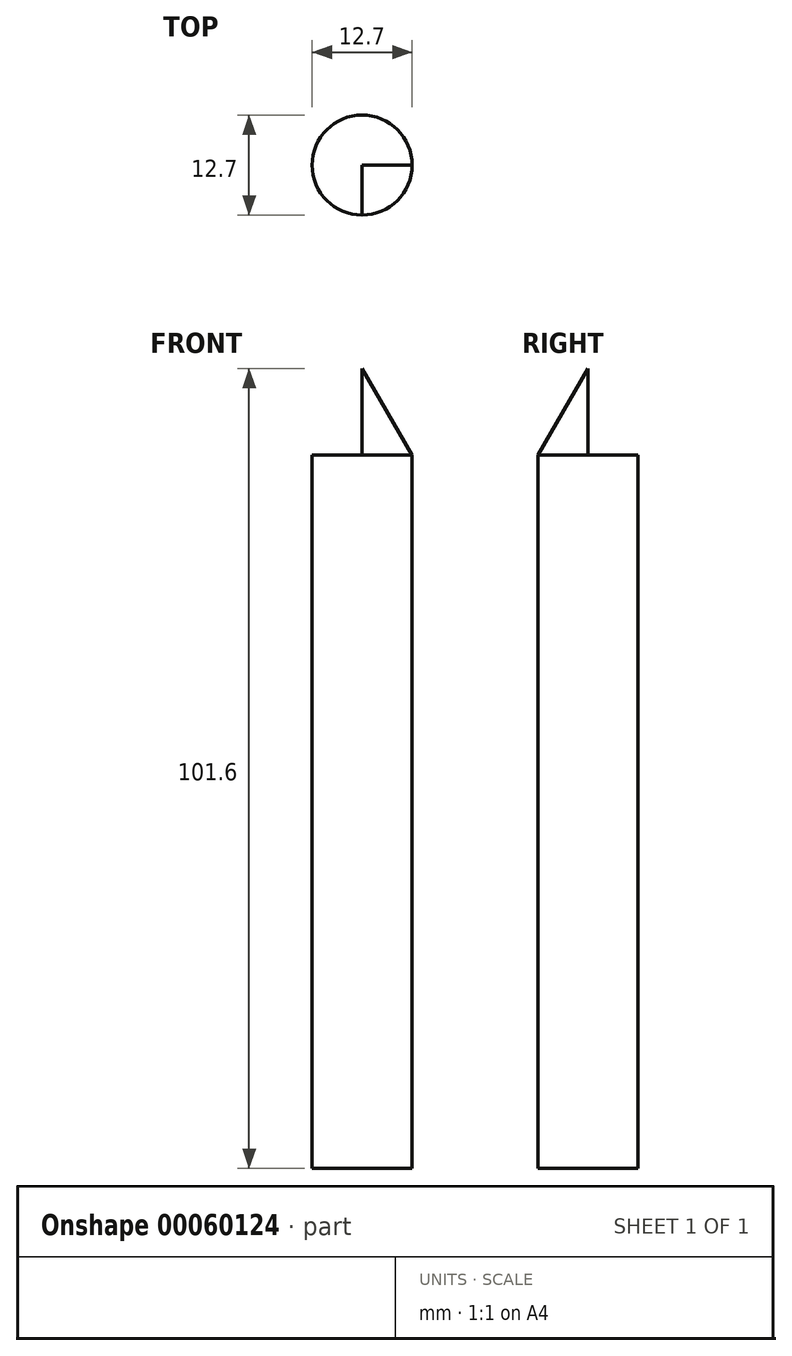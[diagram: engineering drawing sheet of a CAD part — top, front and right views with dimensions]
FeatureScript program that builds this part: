
annotation { "Feature Type Name" : "Feature", "Feature Type Description" : "" }
export const myFeature = defineFeature(function(context is Context, id is Id, definition is map)
    precondition{}
    {
        {
            var Q0;
            Q0=qCreatedBy(makeId("Top.planeOp"),FACE);
            var sketch = newSketch(context, id + "F0", { "sketchPlane" : qUnion([Q0])});
            skCircle(sketch, "E0", {"center": v(0, 0) * mm, "radius": 6.35 * mm});
            skSolve(sketch);
        }
        {
            var Q0;
            Q0 = qSketchRegion(id + "F0", true);
            extrude(context, id + "F1", {"entities" : qUnion([Q0]), "depth" : 50.8 * mm, "hasSecondDirection" : true, "secondDirectionOppositeDirection" : true, "secondDirectionDepth" : 50.8 * mm});
        }
        {
            var Q0;
            Q0=qCreatedBy(makeId("Right.planeOp"),FACE);
            var sketch = newSketch(context, id + "F2", { "sketchPlane" : qUnion([Q0])});
            skLineSegment(sketch, "E1", {"start": v(0, 50.8) * mm, "end": v(-6.35, 39.8) * mm});
            skLineSegment(sketch, "E2", {"start": v(0, 50.8) * mm, "end": v(0, 0) * mm, "construction": true});
            skLineSegment(sketch, "E3", {"start": v(4.5, 58.61) * mm, "end": v(-13.66, 27.15) * mm});
            skLineSegment(sketch, "E4", {"start": v(-13.66, 27.15) * mm, "end": v(-13.66, 58.61) * mm});
            skLineSegment(sketch, "E5", {"start": v(-13.66, 58.61) * mm, "end": v(4.5, 58.61) * mm});
            skLineSegment(sketch, "E6", {"start": v(0, 50.8) * mm, "end": v(0, 58.61) * mm});
            skSolve(sketch);
        }
        {
            var Q0;
            {var subQ0=sQuery(id+"F2.wireOp",EDGE,"E4");Q0=makeQuery(id+"F2.imprint","IMPRINT",FACE,{"disambiguationData":[TD([[makeQuery(id+"F2.imprint","IMPRINT",EDGE,{"derivedFrom":subQ0}),-1.0]])]});}
            var Q1;
            Q1=sQuery(id+"F2.wireOp",EDGE,"E2");
            revolve(context, id + "F3", {"operationType" : NewBodyOperationType.REMOVE, "entities" : qUnion([Q0]), "axis" : qUnion([Q1]), "revolveType" : RevolveType.FULL, "oppositeDirection" : true});
        }
        {
            var Q0;
            Q0 = qSketchRegion(id + "F2", true);
            var sketch = newSketch(context, id + "F4", { "sketchPlane" : qUnion([Q0])});
            skLineSegment(sketch, "E7.bottom", {"start": v(0, 35) * mm, "end": v(0, 35) * mm});
            skLineSegment(sketch, "E7.top", {"start": v(0, 56.46) * mm, "end": v(0, 56.46) * mm});
            skLineSegment(sketch, "E8.bottom", {"start": v(0, 39.8) * mm, "end": v(-6.35, 39.8) * mm});
            skLineSegment(sketch, "E8.top", {"start": v(0, 57.8) * mm, "end": v(-6.35, 57.8) * mm});
            skLineSegment(sketch, "E8.left", {"start": v(0, 39.8) * mm, "end": v(0, 57.8) * mm});
            skLineSegment(sketch, "E8.right", {"start": v(-6.35, 39.8) * mm, "end": v(-6.35, 57.8) * mm});
            skSolve(sketch);
        }
        {
            var Q0;
            Q0 = qSketchRegion(id + "F4", true);
            var Q1;
            Q1=sQuery(id+"F4.wireOp",EDGE,"E8.left");
            revolve(context, id + "F5", {"operationType" : NewBodyOperationType.REMOVE, "entities" : qUnion([Q0]), "axis" : qUnion([Q1]), "revolveType" : RevolveType.ONE_DIRECTION, "oppositeDirection" : true, "angle" : 270 * degree});
        }
    });
